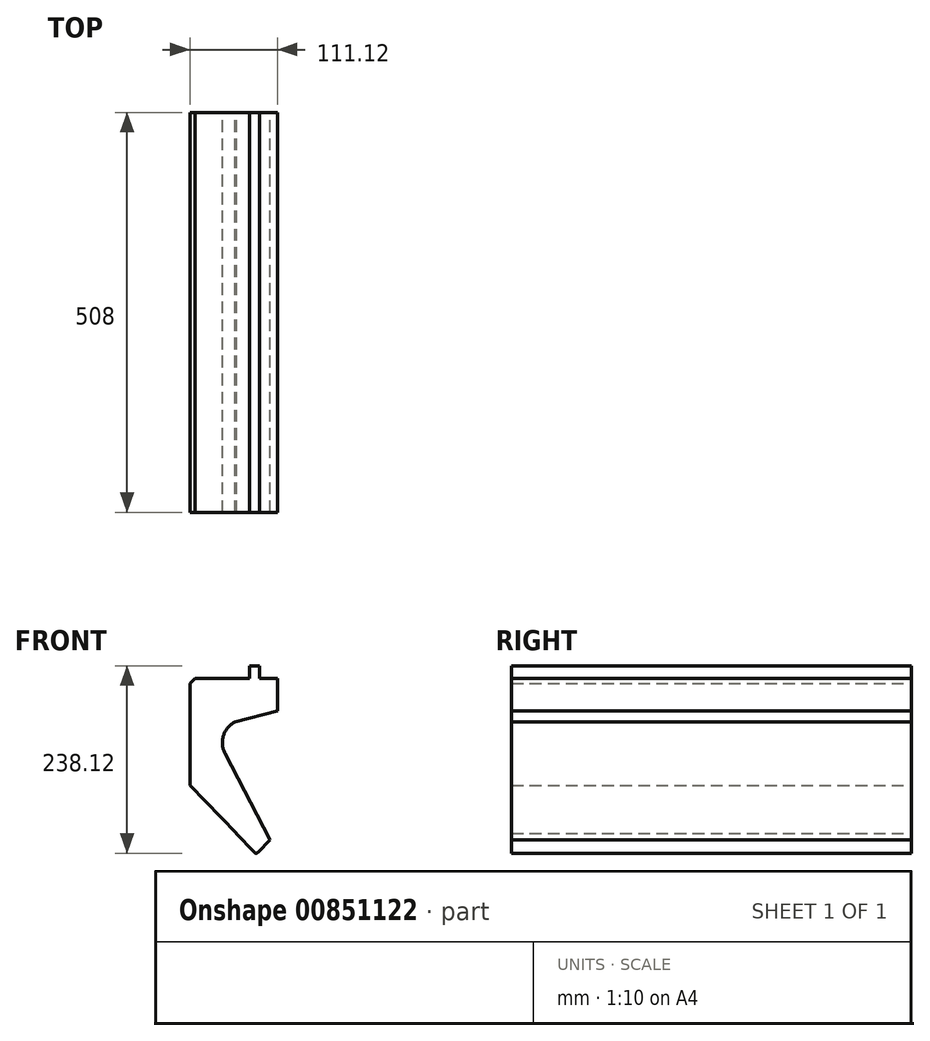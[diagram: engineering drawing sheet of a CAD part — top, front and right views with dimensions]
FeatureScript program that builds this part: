
annotation { "Feature Type Name" : "Feature", "Feature Type Description" : "" }
export const myFeature = defineFeature(function(context is Context, id is Id, definition is map)
    precondition{}
    {
        {
            var Q0;
            Q0=qCreatedBy(makeId("Front.planeOp"),FACE);
            var sketch = newSketch(context, id + "F0", { "sketchPlane" : qUnion([Q0])});
            skLineSegment(sketch, "E0", {"start": v(0, 215.9) * mm, "end": v(0, 86.4) * mm});
            skLineSegment(sketch, "E1", {"start": v(0, 86.4) * mm, "end": v(58.9, 25.4) * mm});
            skLineSegment(sketch, "E2", {"start": v(58.9, 25.4) * mm, "end": v(58.54, 25.04) * mm});
            skLineSegment(sketch, "E3", {"start": v(58.54, 25.04) * mm, "end": v(81.8, 0.97) * mm});
            skLineSegment(sketch, "E4", {"start": v(86.36, 0.97) * mm, "end": v(101.65, 16.8) * mm});
            skLineSegment(sketch, "E5", {"start": v(101.65, 16.8) * mm, "end": v(44.45, 127) * mm});
            skLineSegment(sketch, "E6", {"start": v(6.35, 222.25) * mm, "end": v(75.44, 222.25) * mm});
            skLineSegment(sketch, "E7", {"start": v(75.44, 222.25) * mm, "end": v(75.44, 238.13) * mm});
            skLineSegment(sketch, "E8", {"start": v(75.44, 238.13) * mm, "end": v(88.14, 238.13) * mm});
            skLineSegment(sketch, "E9", {"start": v(88.14, 238.13) * mm, "end": v(88.14, 222.25) * mm});
            skLineSegment(sketch, "E10", {"start": v(88.14, 222.25) * mm, "end": v(111.13, 222.25) * mm});
            skLineSegment(sketch, "E11", {"start": v(111.13, 222.25) * mm, "end": v(111.13, 180.98) * mm});
            skLineSegment(sketch, "E12", {"start": v(111.12, 180.98) * mm, "end": v(57.15, 166.67) * mm});
            skPoint(sketch, "E13.visualSharp", {"position": v(84.07, -1.4) * mm});
            skArc(sketch, "E13.filletArc", {"start": v(81.8, 0.97) * mm, "mid": v(84.07, 0) * mm, "end": v(86.36, 0.97) * mm});
            skArc(sketch, "E14", {"start": v(57.15, 166.67) * mm, "mid": v(42.55, 149.48) * mm, "end": v(44.45, 127) * mm});
            skLineSegment(sketch, "E15", {"start": v(6.35, 222.25) * mm, "end": v(0, 215.9) * mm});
            skPoint(sketch, "E16.orphan", {"position": v(0, 222.25) * mm});
            skSolve(sketch);
        }
        {
            var Q0;
            Q0 = qSketchRegion(id + "F0", true);
            extrude(context, id + "F1", {"entities" : qUnion([Q0]), "depth" : 254 * mm, "offsetDistance" : 25.4 * mm, "hasSecondDirection" : true, "secondDirectionOppositeDirection" : true, "secondDirectionDepth" : 254 * mm});
        }
    });
